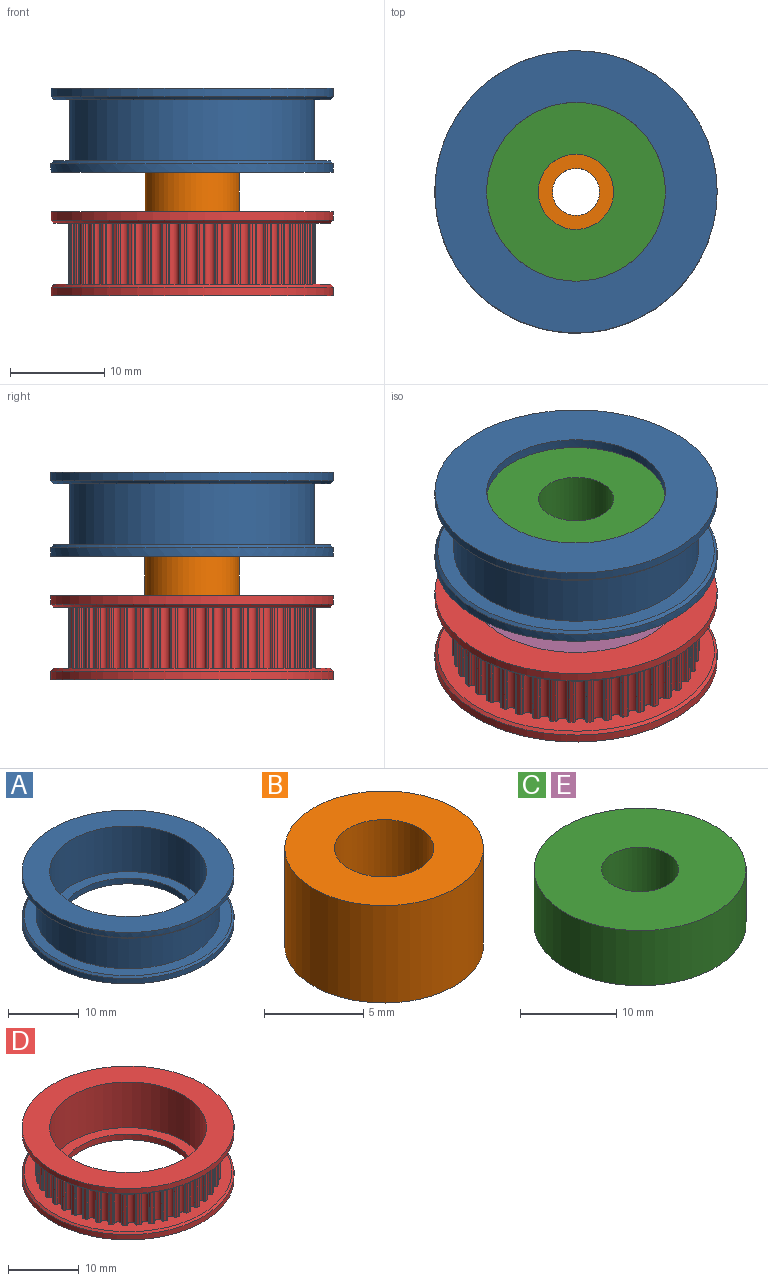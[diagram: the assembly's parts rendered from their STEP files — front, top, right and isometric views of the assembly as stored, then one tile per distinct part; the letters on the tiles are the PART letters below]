
ASSEMBLY  parts=5 mates=4
PART A: 12 faces, bbox 30x30x8.9 mm
  f0: plane 30x30mm, normal (0,0,1), area 319.8mm2, adj f6,f8
  f1: plane 30x30mm, normal (0,0,-1), area 423.3mm2, adj f2,f7
  f2: cylinder r=15mm len=30mm, axis (0,0,1), area 84.8mm2, adj f1,f11
  f3: plane 29.4x29.4mm, normal (0,0,1), area 147.9mm2, adj f4,f11
  f4: cylinder r=13mm len=26mm, axis (0,0,1), area 530.9mm2, adj f3,f5
  f5: plane 29.4x29.4mm, normal (0,0,-1), area 147.9mm2, adj f4,f10
  f6: cylinder r=15mm len=30mm, axis (0,0,1), area 84.8mm2, adj f0,f10
  f7: cylinder r=9.5mm len=19mm, axis (0,0,1), area 59.7mm2, adj f1,f9
  f8: cylinder r=11.1mm len=22.2mm, axis (0,0,1), area 551mm2, adj f0,f9
  f9: plane 22.2x22.2mm, normal (0,0,1), area 103.5mm2, adj f7,f8
  f10: cone r=15mm half-angle=45deg, axis (0,0,1), area 39.6mm2, adj f5,f6
  f11: cone r=14.7mm half-angle=45deg, axis (0,0,-1), area 39.6mm2, adj f2,f3
PART B: 4 faces, bbox 10x10x6 mm
  f0: cylinder r=2.5mm len=6mm, axis (0,0,-1), area 94.2mm2, adj f2,f3
  f1: cylinder r=5mm len=10mm, axis (0,0,-1), area 188.5mm2, adj f2,f3
  f2: plane 10x10mm, normal (0,0,1), area 58.9mm2, adj f0,f1
  f3: plane 10x10mm, normal (0,0,-1), area 58.9mm2, adj f0,f1
PART C: 4 faces, bbox 22x22x7 mm
  f0: cylinder r=4mm len=8mm, axis (0,0,-1), area 175.9mm2, adj f2,f3
  f1: cylinder r=11mm len=22mm, axis (0,0,-1), area 483.8mm2, adj f2,f3
  f2: plane 22x22mm, normal (0,0,1), area 329.9mm2, adj f0,f1
  f3: plane 22x22mm, normal (0,0,-1), area 329.9mm2, adj f0,f1
PART D: 263 faces, bbox 30x30x8.9 mm
  f0: cylinder r=13.12mm len=6.5mm, axis (0,0,-1), area 2.7mm2, adj f1,f12,f252,f255
  f1: cylinder r=0.19mm len=6.5mm, axis (0,0,-1), area 1.7mm2, adj f0,f2,f252,f255
  f2: cylinder r=5mm len=6.5mm, axis (0,0,-1), area 1.2mm2, adj f1,f3,f252,f255
  f3: cylinder r=0.56mm len=6.5mm, axis (0,0,-1), area 9.4mm2, adj f2,f4,f252,f255
  f4: cylinder r=5mm len=6.5mm, axis (0,0,-1), area 1.2mm2, adj f3,f5,f252,f255
  f5: cylinder r=0.19mm len=6.5mm, axis (0,0,-1), area 1.7mm2, adj f4,f6,f252,f255
  f6: cylinder r=13.12mm len=6.5mm, axis (0,0,-1), area 2.7mm2, adj f5,f247,f252,f255
  f7: cylinder r=13.12mm len=6.5mm, axis (0,0,-1), area 2.7mm2, adj f8,f18,f252,f255
  f8: cylinder r=0.19mm len=6.5mm, axis (0,0,-1), area 1.7mm2, adj f7,f9,f252,f255
  f9: cylinder r=5mm len=6.5mm, axis (0,0,-1), area 1.2mm2, adj f8,f10,f252,f255
  f10: cylinder r=0.56mm len=6.5mm, axis (0,0,-1), area 9.4mm2, adj f9,f11,f252,f255
  f11: cylinder r=5mm len=6.5mm, axis (0,0,-1), area 1.2mm2, adj f10,f12,f252,f255
  f12: cylinder r=0.19mm len=6.5mm, axis (0,0,-1), area 1.7mm2, adj f0,f11,f252,f255
  f13: cylinder r=13.12mm len=6.5mm, axis (0,0,-1), area 2.7mm2, adj f14,f24,f252,f255
  f14: cylinder r=0.19mm len=6.5mm, axis (0,0,-1), area 1.7mm2, adj f13,f15,f252,f255
  f15: cylinder r=5mm len=6.5mm, axis (0,0,-1), area 1.2mm2, adj f14,f16,f252,f255
  f16: cylinder r=0.56mm len=6.5mm, axis (0,0,-1), area 9.4mm2, adj f15,f17,f252,f255
  f17: cylinder r=5mm len=6.5mm, axis (0,0,-1), area 1.2mm2, adj f16,f18,f252,f255
  f18: cylinder r=0.19mm len=6.5mm, axis (0,0,-1), area 1.7mm2, adj f7,f17,f252,f255
  f19: cylinder r=13.12mm len=6.5mm, axis (0,0,-1), area 2.7mm2, adj f20,f30,f252,f255
  f20: cylinder r=0.19mm len=6.5mm, axis (0,0,-1), area 1.7mm2, adj f19,f21,f252,f255
  f21: cylinder r=5mm len=6.5mm, axis (0,0,-1), area 1.2mm2, adj f20,f22,f252,f255
  f22: cylinder r=0.56mm len=6.5mm, axis (0,0,-1), area 9.4mm2, adj f21,f23,f252,f255
  f23: cylinder r=5mm len=6.5mm, axis (0,0,-1), area 1.2mm2, adj f22,f24,f252,f255
  f24: cylinder r=0.19mm len=6.5mm, axis (0,0,-1), area 1.7mm2, adj f13,f23,f252,f255
  f25: cylinder r=13.12mm len=6.5mm, axis (0,0,-1), area 2.7mm2, adj f26,f36,f252,f255
  f26: cylinder r=0.19mm len=6.5mm, axis (0,0,-1), area 1.7mm2, adj f25,f27,f252,f255
  f27: cylinder r=5mm len=6.5mm, axis (0,0,-1), area 1.2mm2, adj f26,f28,f252,f255
  f28: cylinder r=0.56mm len=6.5mm, axis (0,0,-1), area 9.4mm2, adj f27,f29,f252,f255
  f29: cylinder r=5mm len=6.5mm, axis (0,0,-1), area 1.2mm2, adj f28,f30,f252,f255
  f30: cylinder r=0.19mm len=6.5mm, axis (0,0,-1), area 1.7mm2, adj f19,f29,f252,f255
  f31: cylinder r=13.12mm len=6.5mm, axis (0,0,-1), area 2.7mm2, adj f32,f42,f252,f255
  f32: cylinder r=0.19mm len=6.5mm, axis (0,0,-1), area 1.7mm2, adj f31,f33,f252,f255
  f33: cylinder r=5mm len=6.5mm, axis (0,0,-1), area 1.2mm2, adj f32,f34,f252,f255
  f34: cylinder r=0.56mm len=6.5mm, axis (0,0,-1), area 9.4mm2, adj f33,f35,f252,f255
  f35: cylinder r=5mm len=6.5mm, axis (0,0,-1), area 1.2mm2, adj f34,f36,f252,f255
  f36: cylinder r=0.19mm len=6.5mm, axis (0,0,-1), area 1.7mm2, adj f25,f35,f252,f255
  f37: cylinder r=13.12mm len=6.5mm, axis (0,0,-1), area 2.7mm2, adj f38,f48,f252,f255
  f38: cylinder r=0.19mm len=6.5mm, axis (0,0,-1), area 1.7mm2, adj f37,f39,f252,f255
  f39: cylinder r=5mm len=6.5mm, axis (0,0,-1), area 1.2mm2, adj f38,f40,f252,f255
  f40: cylinder r=0.56mm len=6.5mm, axis (0,0,-1), area 9.4mm2, adj f39,f41,f252,f255
  f41: cylinder r=5mm len=6.5mm, axis (0,0,-1), area 1.2mm2, adj f40,f42,f252,f255
  f42: cylinder r=0.19mm len=6.5mm, axis (0,0,-1), area 1.7mm2, adj f31,f41,f252,f255
  f43: cylinder r=13.12mm len=6.5mm, axis (0,0,-1), area 2.7mm2, adj f44,f54,f252,f255
  f44: cylinder r=0.19mm len=6.5mm, axis (0,0,-1), area 1.7mm2, adj f43,f45,f252,f255
  f45: cylinder r=5mm len=6.5mm, axis (0,0,-1), area 1.2mm2, adj f44,f46,f252,f255
  f46: cylinder r=0.56mm len=6.5mm, axis (0,0,-1), area 9.4mm2, adj f45,f47,f252,f255
  f47: cylinder r=5mm len=6.5mm, axis (0,0,-1), area 1.2mm2, adj f46,f48,f252,f255
  f48: cylinder r=0.19mm len=6.5mm, axis (0,0,-1), area 1.7mm2, adj f37,f47,f252,f255
  f49: cylinder r=13.12mm len=6.5mm, axis (0,0,-1), area 2.7mm2, adj f50,f60,f252,f255
  f50: cylinder r=0.19mm len=6.5mm, axis (0,0,-1), area 1.7mm2, adj f49,f51,f252,f255
  f51: cylinder r=5mm len=6.5mm, axis (0,0,-1), area 1.2mm2, adj f50,f52,f252,f255
  f52: cylinder r=0.56mm len=6.5mm, axis (0,0,-1), area 9.4mm2, adj f51,f53,f252,f255
  f53: cylinder r=5mm len=6.5mm, axis (0,0,-1), area 1.2mm2, adj f52,f54,f252,f255
  f54: cylinder r=0.19mm len=6.5mm, axis (0,0,-1), area 1.7mm2, adj f43,f53,f252,f255
  f55: cylinder r=13.12mm len=6.5mm, axis (0,0,-1), area 2.7mm2, adj f56,f66,f252,f255
  f56: cylinder r=0.19mm len=6.5mm, axis (0,0,-1), area 1.7mm2, adj f55,f57,f252,f255
  f57: cylinder r=5mm len=6.5mm, axis (0,0,-1), area 1.2mm2, adj f56,f58,f252,f255
  f58: cylinder r=0.56mm len=6.5mm, axis (0,0,-1), area 9.4mm2, adj f57,f59,f252,f255
  f59: cylinder r=5mm len=6.5mm, axis (0,0,-1), area 1.2mm2, adj f58,f60,f252,f255
  f60: cylinder r=0.19mm len=6.5mm, axis (0,0,-1), area 1.7mm2, adj f49,f59,f252,f255
  f61: cylinder r=13.12mm len=6.5mm, axis (0,0,-1), area 2.7mm2, adj f62,f72,f252,f255
  f62: cylinder r=0.19mm len=6.5mm, axis (0,0,-1), area 1.7mm2, adj f61,f63,f252,f255
  f63: cylinder r=5mm len=6.5mm, axis (0,0,-1), area 1.2mm2, adj f62,f64,f252,f255
  f64: cylinder r=0.56mm len=6.5mm, axis (0,0,-1), area 9.4mm2, adj f63,f65,f252,f255
  f65: cylinder r=5mm len=6.5mm, axis (0,0,-1), area 1.2mm2, adj f64,f66,f252,f255
  f66: cylinder r=0.19mm len=6.5mm, axis (0,0,-1), area 1.7mm2, adj f55,f65,f252,f255
  f67: cylinder r=13.12mm len=6.5mm, axis (0,0,-1), area 2.7mm2, adj f68,f78,f252,f255
  f68: cylinder r=0.19mm len=6.5mm, axis (0,0,-1), area 1.7mm2, adj f67,f69,f252,f255
  f69: cylinder r=5mm len=6.5mm, axis (0,0,-1), area 1.2mm2, adj f68,f70,f252,f255
  f70: cylinder r=0.56mm len=6.5mm, axis (0,0,-1), area 9.4mm2, adj f69,f71,f252,f255
  f71: cylinder r=5mm len=6.5mm, axis (0,0,-1), area 1.2mm2, adj f70,f72,f252,f255
  f72: cylinder r=0.19mm len=6.5mm, axis (0,0,-1), area 1.7mm2, adj f61,f71,f252,f255
  f73: cylinder r=13.12mm len=6.5mm, axis (0,0,-1), area 2.7mm2, adj f74,f84,f252,f255
  f74: cylinder r=0.19mm len=6.5mm, axis (0,0,-1), area 1.7mm2, adj f73,f75,f252,f255
  f75: cylinder r=5mm len=6.5mm, axis (0,0,-1), area 1.2mm2, adj f74,f76,f252,f255
  f76: cylinder r=0.56mm len=6.5mm, axis (0,0,-1), area 9.4mm2, adj f75,f77,f252,f255
  f77: cylinder r=5mm len=6.5mm, axis (0,0,-1), area 1.2mm2, adj f76,f78,f252,f255
  f78: cylinder r=0.19mm len=6.5mm, axis (0,0,-1), area 1.7mm2, adj f67,f77,f252,f255
  f79: cylinder r=13.12mm len=6.5mm, axis (0,0,-1), area 2.7mm2, adj f80,f90,f252,f255
  f80: cylinder r=0.19mm len=6.5mm, axis (0,0,-1), area 1.7mm2, adj f79,f81,f252,f255
  f81: cylinder r=5mm len=6.5mm, axis (0,0,-1), area 1.2mm2, adj f80,f82,f252,f255
  f82: cylinder r=0.56mm len=6.5mm, axis (0,0,-1), area 9.4mm2, adj f81,f83,f252,f255
  f83: cylinder r=5mm len=6.5mm, axis (0,0,-1), area 1.2mm2, adj f82,f84,f252,f255
  f84: cylinder r=0.19mm len=6.5mm, axis (0,0,-1), area 1.7mm2, adj f73,f83,f252,f255
  f85: cylinder r=13.12mm len=6.5mm, axis (0,0,-1), area 2.7mm2, adj f86,f96,f252,f255
  f86: cylinder r=0.19mm len=6.5mm, axis (0,0,-1), area 1.7mm2, adj f85,f87,f252,f255
  f87: cylinder r=5mm len=6.5mm, axis (0,0,-1), area 1.2mm2, adj f86,f88,f252,f255
  f88: cylinder r=0.56mm len=6.5mm, axis (0,0,-1), area 9.4mm2, adj f87,f89,f252,f255
  f89: cylinder r=5mm len=6.5mm, axis (0,0,-1), area 1.2mm2, adj f88,f90,f252,f255
  f90: cylinder r=0.19mm len=6.5mm, axis (0,0,-1), area 1.7mm2, adj f79,f89,f252,f255
  f91: cylinder r=13.12mm len=6.5mm, axis (0,0,-1), area 2.7mm2, adj f92,f102,f252,f255
  f92: cylinder r=0.19mm len=6.5mm, axis (0,0,-1), area 1.7mm2, adj f91,f93,f252,f255
  f93: cylinder r=5mm len=6.5mm, axis (0,0,-1), area 1.2mm2, adj f92,f94,f252,f255
  f94: cylinder r=0.56mm len=6.5mm, axis (0,0,-1), area 9.4mm2, adj f93,f95,f252,f255
  f95: cylinder r=5mm len=6.5mm, axis (0,0,-1), area 1.2mm2, adj f94,f96,f252,f255
  f96: cylinder r=0.19mm len=6.5mm, axis (0,0,-1), area 1.7mm2, adj f85,f95,f252,f255
  f97: cylinder r=13.12mm len=6.5mm, axis (0,0,-1), area 2.7mm2, adj f98,f108,f252,f255
  f98: cylinder r=0.19mm len=6.5mm, axis (0,0,-1), area 1.7mm2, adj f97,f99,f252,f255
  f99: cylinder r=5mm len=6.5mm, axis (0,0,-1), area 1.2mm2, adj f98,f100,f252,f255
  f100: cylinder r=0.56mm len=6.5mm, axis (0,0,-1), area 9.4mm2, adj f99,f101,f252,f255
  f101: cylinder r=5mm len=6.5mm, axis (0,0,-1), area 1.2mm2, adj f100,f102,f252,f255
  f102: cylinder r=0.19mm len=6.5mm, axis (0,0,-1), area 1.7mm2, adj f91,f101,f252,f255
  f103: cylinder r=13.12mm len=6.5mm, axis (0,0,-1), area 2.7mm2, adj f104,f114,f252,f255
  f104: cylinder r=0.19mm len=6.5mm, axis (0,0,-1), area 1.7mm2, adj f103,f105,f252,f255
  f105: cylinder r=5mm len=6.5mm, axis (0,0,-1), area 1.2mm2, adj f104,f106,f252,f255
  f106: cylinder r=0.56mm len=6.5mm, axis (0,0,-1), area 9.4mm2, adj f105,f107,f252,f255
  f107: cylinder r=5mm len=6.5mm, axis (0,0,-1), area 1.2mm2, adj f106,f108,f252,f255
  f108: cylinder r=0.19mm len=6.5mm, axis (0,0,-1), area 1.7mm2, adj f97,f107,f252,f255
  f109: cylinder r=13.12mm len=6.5mm, axis (0,0,-1), area 2.7mm2, adj f110,f120,f252,f255
  f110: cylinder r=0.19mm len=6.5mm, axis (0,0,-1), area 1.7mm2, adj f109,f111,f252,f255
  f111: cylinder r=5mm len=6.5mm, axis (0,0,-1), area 1.2mm2, adj f110,f112,f252,f255
  f112: cylinder r=0.56mm len=6.5mm, axis (0,0,-1), area 9.4mm2, adj f111,f113,f252,f255
  f113: cylinder r=5mm len=6.5mm, axis (0,0,-1), area 1.2mm2, adj f112,f114,f252,f255
  f114: cylinder r=0.19mm len=6.5mm, axis (0,0,-1), area 1.7mm2, adj f103,f113,f252,f255
  f115: cylinder r=13.12mm len=6.5mm, axis (0,0,-1), area 2.7mm2, adj f116,f126,f252,f255
  f116: cylinder r=0.19mm len=6.5mm, axis (0,0,-1), area 1.7mm2, adj f115,f117,f252,f255
  f117: cylinder r=5mm len=6.5mm, axis (0,0,-1), area 1.2mm2, adj f116,f118,f252,f255
  f118: cylinder r=0.56mm len=6.5mm, axis (0,0,-1), area 9.4mm2, adj f117,f119,f252,f255
  f119: cylinder r=5mm len=6.5mm, axis (0,0,-1), area 1.2mm2, adj f118,f120,f252,f255
  f120: cylinder r=0.19mm len=6.5mm, axis (0,0,-1), area 1.7mm2, adj f109,f119,f252,f255
  f121: cylinder r=13.12mm len=6.5mm, axis (0,0,-1), area 2.7mm2, adj f122,f132,f252,f255
  f122: cylinder r=0.19mm len=6.5mm, axis (0,0,-1), area 1.7mm2, adj f121,f123,f252,f255
  f123: cylinder r=5mm len=6.5mm, axis (0,0,-1), area 1.2mm2, adj f122,f124,f252,f255
  f124: cylinder r=0.56mm len=6.5mm, axis (0,0,-1), area 9.4mm2, adj f123,f125,f252,f255
  f125: cylinder r=5mm len=6.5mm, axis (0,0,-1), area 1.2mm2, adj f124,f126,f252,f255
  f126: cylinder r=0.19mm len=6.5mm, axis (0,0,-1), area 1.7mm2, adj f115,f125,f252,f255
  f127: cylinder r=13.12mm len=6.5mm, axis (0,0,-1), area 2.7mm2, adj f128,f138,f252,f255
  f128: cylinder r=0.19mm len=6.5mm, axis (0,0,-1), area 1.7mm2, adj f127,f129,f252,f255
  f129: cylinder r=5mm len=6.5mm, axis (0,0,-1), area 1.2mm2, adj f128,f130,f252,f255
  f130: cylinder r=0.56mm len=6.5mm, axis (0,0,-1), area 9.4mm2, adj f129,f131,f252,f255
  f131: cylinder r=5mm len=6.5mm, axis (0,0,-1), area 1.2mm2, adj f130,f132,f252,f255
  f132: cylinder r=0.19mm len=6.5mm, axis (0,0,-1), area 1.7mm2, adj f121,f131,f252,f255
  f133: cylinder r=13.12mm len=6.5mm, axis (0,0,-1), area 2.7mm2, adj f134,f144,f252,f255
  f134: cylinder r=0.19mm len=6.5mm, axis (0,0,-1), area 1.7mm2, adj f133,f135,f252,f255
  f135: cylinder r=5mm len=6.5mm, axis (0,0,-1), area 1.2mm2, adj f134,f136,f252,f255
  f136: cylinder r=0.56mm len=6.5mm, axis (0,0,-1), area 9.4mm2, adj f135,f137,f252,f255
  f137: cylinder r=5mm len=6.5mm, axis (0,0,-1), area 1.2mm2, adj f136,f138,f252,f255
  f138: cylinder r=0.19mm len=6.5mm, axis (0,0,-1), area 1.7mm2, adj f127,f137,f252,f255
  f139: cylinder r=13.12mm len=6.5mm, axis (0,0,-1), area 2.7mm2, adj f140,f150,f252,f255
  f140: cylinder r=0.19mm len=6.5mm, axis (0,0,-1), area 1.7mm2, adj f139,f141,f252,f255
  f141: cylinder r=5mm len=6.5mm, axis (0,0,-1), area 1.2mm2, adj f140,f142,f252,f255
  f142: cylinder r=0.56mm len=6.5mm, axis (0,0,-1), area 9.4mm2, adj f141,f143,f252,f255
  f143: cylinder r=5mm len=6.5mm, axis (0,0,-1), area 1.2mm2, adj f142,f144,f252,f255
  f144: cylinder r=0.19mm len=6.5mm, axis (0,0,-1), area 1.7mm2, adj f133,f143,f252,f255
  f145: cylinder r=13.12mm len=6.5mm, axis (0,0,-1), area 2.7mm2, adj f146,f156,f252,f255
  f146: cylinder r=0.19mm len=6.5mm, axis (0,0,-1), area 1.7mm2, adj f145,f147,f252,f255
  f147: cylinder r=5mm len=6.5mm, axis (0,0,-1), area 1.2mm2, adj f146,f148,f252,f255
  f148: cylinder r=0.56mm len=6.5mm, axis (0,0,-1), area 9.4mm2, adj f147,f149,f252,f255
  f149: cylinder r=5mm len=6.5mm, axis (0,0,-1), area 1.2mm2, adj f148,f150,f252,f255
  f150: cylinder r=0.19mm len=6.5mm, axis (0,0,-1), area 1.7mm2, adj f139,f149,f252,f255
  f151: cylinder r=13.12mm len=6.5mm, axis (0,0,-1), area 2.7mm2, adj f152,f162,f252,f255
  f152: cylinder r=0.19mm len=6.5mm, axis (0,0,-1), area 1.7mm2, adj f151,f153,f252,f255
  f153: cylinder r=5mm len=6.5mm, axis (0,0,-1), area 1.2mm2, adj f152,f154,f252,f255
  f154: cylinder r=0.56mm len=6.5mm, axis (0,0,-1), area 9.4mm2, adj f153,f155,f252,f255
  f155: cylinder r=5mm len=6.5mm, axis (0,0,-1), area 1.2mm2, adj f154,f156,f252,f255
  f156: cylinder r=0.19mm len=6.5mm, axis (0,0,-1), area 1.7mm2, adj f145,f155,f252,f255
  f157: cylinder r=13.12mm len=6.5mm, axis (0,0,-1), area 2.7mm2, adj f158,f168,f252,f255
  f158: cylinder r=0.19mm len=6.5mm, axis (0,0,-1), area 1.7mm2, adj f157,f159,f252,f255
  f159: cylinder r=5mm len=6.5mm, axis (0,0,-1), area 1.2mm2, adj f158,f160,f252,f255
  f160: cylinder r=0.56mm len=6.5mm, axis (0,0,-1), area 9.4mm2, adj f159,f161,f252,f255
  f161: cylinder r=5mm len=6.5mm, axis (0,0,-1), area 1.2mm2, adj f160,f162,f252,f255
  f162: cylinder r=0.19mm len=6.5mm, axis (0,0,-1), area 1.7mm2, adj f151,f161,f252,f255
  f163: cylinder r=13.12mm len=6.5mm, axis (0,0,-1), area 2.7mm2, adj f164,f174,f252,f255
  f164: cylinder r=0.19mm len=6.5mm, axis (0,0,-1), area 1.7mm2, adj f163,f165,f252,f255
  f165: cylinder r=5mm len=6.5mm, axis (0,0,-1), area 1.2mm2, adj f164,f166,f252,f255
  f166: cylinder r=0.56mm len=6.5mm, axis (0,0,-1), area 9.4mm2, adj f165,f167,f252,f255
  f167: cylinder r=5mm len=6.5mm, axis (0,0,-1), area 1.2mm2, adj f166,f168,f252,f255
  f168: cylinder r=0.19mm len=6.5mm, axis (0,0,-1), area 1.7mm2, adj f157,f167,f252,f255
  f169: cylinder r=13.12mm len=6.5mm, axis (0,0,-1), area 2.7mm2, adj f170,f180,f252,f255
  f170: cylinder r=0.19mm len=6.5mm, axis (0,0,-1), area 1.7mm2, adj f169,f171,f252,f255
  f171: cylinder r=5mm len=6.5mm, axis (0,0,-1), area 1.2mm2, adj f170,f172,f252,f255
  f172: cylinder r=0.56mm len=6.5mm, axis (0,0,-1), area 9.4mm2, adj f171,f173,f252,f255
  f173: cylinder r=5mm len=6.5mm, axis (0,0,-1), area 1.2mm2, adj f172,f174,f252,f255
  f174: cylinder r=0.19mm len=6.5mm, axis (0,0,-1), area 1.7mm2, adj f163,f173,f252,f255
  f175: cylinder r=13.12mm len=6.5mm, axis (0,0,-1), area 2.7mm2, adj f176,f186,f252,f255
  f176: cylinder r=0.19mm len=6.5mm, axis (0,0,-1), area 1.7mm2, adj f175,f177,f252,f255
  f177: cylinder r=5mm len=6.5mm, axis (0,0,-1), area 1.2mm2, adj f176,f178,f252,f255
  f178: cylinder r=0.56mm len=6.5mm, axis (0,0,-1), area 9.4mm2, adj f177,f179,f252,f255
  f179: cylinder r=5mm len=6.5mm, axis (0,0,-1), area 1.2mm2, adj f178,f180,f252,f255
  f180: cylinder r=0.19mm len=6.5mm, axis (0,0,-1), area 1.7mm2, adj f169,f179,f252,f255
  f181: cylinder r=13.12mm len=6.5mm, axis (0,0,-1), area 2.7mm2, adj f182,f192,f252,f255
  f182: cylinder r=0.19mm len=6.5mm, axis (0,0,-1), area 1.7mm2, adj f181,f183,f252,f255
  f183: cylinder r=5mm len=6.5mm, axis (0,0,-1), area 1.2mm2, adj f182,f184,f252,f255
  f184: cylinder r=0.56mm len=6.5mm, axis (0,0,-1), area 9.4mm2, adj f183,f185,f252,f255
  f185: cylinder r=5mm len=6.5mm, axis (0,0,-1), area 1.2mm2, adj f184,f186,f252,f255
  f186: cylinder r=0.19mm len=6.5mm, axis (0,0,-1), area 1.7mm2, adj f175,f185,f252,f255
  f187: cylinder r=13.12mm len=6.5mm, axis (0,0,-1), area 2.7mm2, adj f188,f198,f252,f255
  f188: cylinder r=0.19mm len=6.5mm, axis (0,0,-1), area 1.7mm2, adj f187,f189,f252,f255
  f189: cylinder r=5mm len=6.5mm, axis (0,0,-1), area 1.2mm2, adj f188,f190,f252,f255
  f190: cylinder r=0.56mm len=6.5mm, axis (0,0,-1), area 9.4mm2, adj f189,f191,f252,f255
  f191: cylinder r=5mm len=6.5mm, axis (0,0,-1), area 1.2mm2, adj f190,f192,f252,f255
  f192: cylinder r=0.19mm len=6.5mm, axis (0,0,-1), area 1.7mm2, adj f181,f191,f252,f255
  f193: cylinder r=13.12mm len=6.5mm, axis (0,0,-1), area 2.7mm2, adj f194,f204,f252,f255
  f194: cylinder r=0.19mm len=6.5mm, axis (0,0,-1), area 1.7mm2, adj f193,f195,f252,f255
  f195: cylinder r=5mm len=6.5mm, axis (0,0,-1), area 1.2mm2, adj f194,f196,f252,f255
  f196: cylinder r=0.56mm len=6.5mm, axis (0,0,-1), area 9.4mm2, adj f195,f197,f252,f255
  f197: cylinder r=5mm len=6.5mm, axis (0,0,-1), area 1.2mm2, adj f196,f198,f252,f255
  f198: cylinder r=0.19mm len=6.5mm, axis (0,0,-1), area 1.7mm2, adj f187,f197,f252,f255
  f199: cylinder r=13.12mm len=6.5mm, axis (0,0,-1), area 2.7mm2, adj f200,f210,f252,f255
  f200: cylinder r=0.19mm len=6.5mm, axis (0,0,-1), area 1.7mm2, adj f199,f201,f252,f255
  f201: cylinder r=5mm len=6.5mm, axis (0,0,-1), area 1.2mm2, adj f200,f202,f252,f255
  f202: cylinder r=0.56mm len=6.5mm, axis (0,0,-1), area 9.4mm2, adj f201,f203,f252,f255
  f203: cylinder r=5mm len=6.5mm, axis (0,0,-1), area 1.2mm2, adj f202,f204,f252,f255
  f204: cylinder r=0.19mm len=6.5mm, axis (0,0,-1), area 1.7mm2, adj f193,f203,f252,f255
  f205: cylinder r=13.12mm len=6.5mm, axis (0,0,-1), area 2.7mm2, adj f206,f216,f252,f255
  f206: cylinder r=0.19mm len=6.5mm, axis (0,0,-1), area 1.7mm2, adj f205,f207,f252,f255
  f207: cylinder r=5mm len=6.5mm, axis (0,0,-1), area 1.2mm2, adj f206,f208,f252,f255
  f208: cylinder r=0.56mm len=6.5mm, axis (0,0,-1), area 9.4mm2, adj f207,f209,f252,f255
  f209: cylinder r=5mm len=6.5mm, axis (0,0,-1), area 1.2mm2, adj f208,f210,f252,f255
  f210: cylinder r=0.19mm len=6.5mm, axis (0,0,-1), area 1.7mm2, adj f199,f209,f252,f255
  f211: cylinder r=13.12mm len=6.5mm, axis (0,0,-1), area 2.7mm2, adj f212,f222,f252,f255
  f212: cylinder r=0.19mm len=6.5mm, axis (0,0,-1), area 1.7mm2, adj f211,f213,f252,f255
  f213: cylinder r=5mm len=6.5mm, axis (0,0,-1), area 1.2mm2, adj f212,f214,f252,f255
  f214: cylinder r=0.56mm len=6.5mm, axis (0,0,-1), area 9.4mm2, adj f213,f215,f252,f255
  f215: cylinder r=5mm len=6.5mm, axis (0,0,-1), area 1.2mm2, adj f214,f216,f252,f255
  f216: cylinder r=0.19mm len=6.5mm, axis (0,0,-1), area 1.7mm2, adj f205,f215,f252,f255
  f217: cylinder r=13.12mm len=6.5mm, axis (0,0,-1), area 2.7mm2, adj f218,f228,f252,f255
  f218: cylinder r=0.19mm len=6.5mm, axis (0,0,-1), area 1.7mm2, adj f217,f219,f252,f255
  f219: cylinder r=5mm len=6.5mm, axis (0,0,-1), area 1.2mm2, adj f218,f220,f252,f255
  f220: cylinder r=0.56mm len=6.5mm, axis (0,0,-1), area 9.4mm2, adj f219,f221,f252,f255
  f221: cylinder r=5mm len=6.5mm, axis (0,0,-1), area 1.2mm2, adj f220,f222,f252,f255
  f222: cylinder r=0.19mm len=6.5mm, axis (0,0,-1), area 1.7mm2, adj f211,f221,f252,f255
  f223: cylinder r=13.12mm len=6.5mm, axis (0,0,-1), area 2.7mm2, adj f224,f234,f252,f255
  f224: cylinder r=0.19mm len=6.5mm, axis (0,0,-1), area 1.7mm2, adj f223,f225,f252,f255
  f225: cylinder r=5mm len=6.5mm, axis (0,0,-1), area 1.2mm2, adj f224,f226,f252,f255
  f226: cylinder r=0.56mm len=6.5mm, axis (0,0,-1), area 9.4mm2, adj f225,f227,f252,f255
  f227: cylinder r=5mm len=6.5mm, axis (0,0,-1), area 1.2mm2, adj f226,f228,f252,f255
  f228: cylinder r=0.19mm len=6.5mm, axis (0,0,-1), area 1.7mm2, adj f217,f227,f252,f255
  f229: cylinder r=13.12mm len=6.5mm, axis (0,0,-1), area 2.7mm2, adj f230,f240,f252,f255
  f230: cylinder r=0.19mm len=6.5mm, axis (0,0,-1), area 1.7mm2, adj f229,f231,f252,f255
  f231: cylinder r=5mm len=6.5mm, axis (0,0,-1), area 1.2mm2, adj f230,f232,f252,f255
  f232: cylinder r=0.56mm len=6.5mm, axis (0,0,-1), area 9.4mm2, adj f231,f233,f252,f255
  f233: cylinder r=5mm len=6.5mm, axis (0,0,-1), area 1.2mm2, adj f232,f234,f252,f255
  f234: cylinder r=0.19mm len=6.5mm, axis (0,0,-1), area 1.7mm2, adj f223,f233,f252,f255
  f235: cylinder r=13.12mm len=6.5mm, axis (0,0,-1), area 2.7mm2, adj f236,f246,f252,f255
  f236: cylinder r=0.19mm len=6.5mm, axis (0,0,-1), area 1.7mm2, adj f235,f237,f252,f255
  f237: cylinder r=5mm len=6.5mm, axis (0,0,-1), area 1.2mm2, adj f236,f238,f252,f255
  f238: cylinder r=0.56mm len=6.5mm, axis (0,0,-1), area 9.4mm2, adj f237,f239,f252,f255
  f239: cylinder r=5mm len=6.5mm, axis (0,0,-1), area 1.2mm2, adj f238,f240,f252,f255
  f240: cylinder r=0.19mm len=6.5mm, axis (0,0,-1), area 1.7mm2, adj f229,f239,f252,f255
  f241: cylinder r=13.12mm len=6.5mm, axis (0,0,-1), area 2.7mm2, adj f242,f251,f252,f255
  f242: cylinder r=0.19mm len=6.5mm, axis (0,0,-1), area 1.7mm2, adj f241,f243,f252,f255
  f243: cylinder r=5mm len=6.5mm, axis (0,0,-1), area 1.2mm2, adj f242,f244,f252,f255
  f244: cylinder r=0.56mm len=6.5mm, axis (0,0,-1), area 9.4mm2, adj f243,f245,f252,f255
  f245: cylinder r=5mm len=6.5mm, axis (0,0,-1), area 1.2mm2, adj f244,f246,f252,f255
  f246: cylinder r=0.19mm len=6.5mm, axis (0,0,-1), area 1.7mm2, adj f235,f245,f252,f255
  f247: cylinder r=0.19mm len=6.5mm, axis (0,0,-1), area 1.7mm2, adj f6,f248,f252,f255
  f248: cylinder r=5mm len=6.5mm, axis (0,0,-1), area 1.2mm2, adj f247,f249,f252,f255
  f249: cylinder r=0.56mm len=6.5mm, axis (0,0,-1), area 9.4mm2, adj f248,f250,f252,f255
  f250: cylinder r=5mm len=6.5mm, axis (0,0,-1), area 1.2mm2, adj f249,f251,f252,f255
  f251: cylinder r=0.19mm len=6.5mm, axis (0,0,-1), area 1.7mm2, adj f241,f250,f252,f255
  f252: plane 29.4x29.4mm, normal (0,0,1), area 168.8mm2, adj f0,f1,f2,f3,f4,f5,f6,f7
  f253: plane 30x30mm, normal (0,0,-1), area 423.3mm2, adj f254,f260
  f254: cylinder r=15mm len=30mm, axis (0,0,1), area 84.8mm2, adj f253,f262
  f255: plane 29.4x29.4mm, normal (0,0,-1), area 168.8mm2, adj f0,f1,f2,f3,f4,f5,f6,f7
  f256: plane 30x30mm, normal (0,0,1), area 319.8mm2, adj f257,f258
  f257: cylinder r=15mm len=30mm, axis (0,0,1), area 84.8mm2, adj f256,f261
  f258: cylinder r=11.1mm len=22.2mm, axis (0,0,1), area 551mm2, adj f256,f259
  f259: plane 22.2x22.2mm, normal (0,0,1), area 103.5mm2, adj f258,f260
  f260: cylinder r=9.5mm len=19mm, axis (0,0,1), area 59.7mm2, adj f253,f259
  f261: cone r=15mm half-angle=45deg, axis (0,0,1), area 39.6mm2, adj f255,f257
  f262: cone r=14.7mm half-angle=45deg, axis (0,0,-1), area 39.6mm2, adj f252,f254
PART E: same geometry as C
PLACE A rot(axis=(1,0,0),180deg) t=(9.21,2.65,32.71)mm
PLACE B t=(9.21,2.65,23.16)mm
PLACE C t=(9.21,2.65,29.16)mm
PLACE D t=(9.21,2.65,19.61)mm
PLACE E t=(9.21,2.65,16.16)mm
MATE fastened D.f0 <-> E.f0  axis (0,0,1) through (9.21,2.65,16.16)mm
MATE fastened A.f7 <-> C.f0  axis (0,0,-1) through (9.21,2.65,36.16)mm
MATE fastened C.f0 <-> B.f0  axis (0,0,-1) through (9.21,2.65,29.16)mm
MATE fastened B.f0 <-> E.f0  axis (0,0,-1) through (9.21,2.65,23.16)mm
